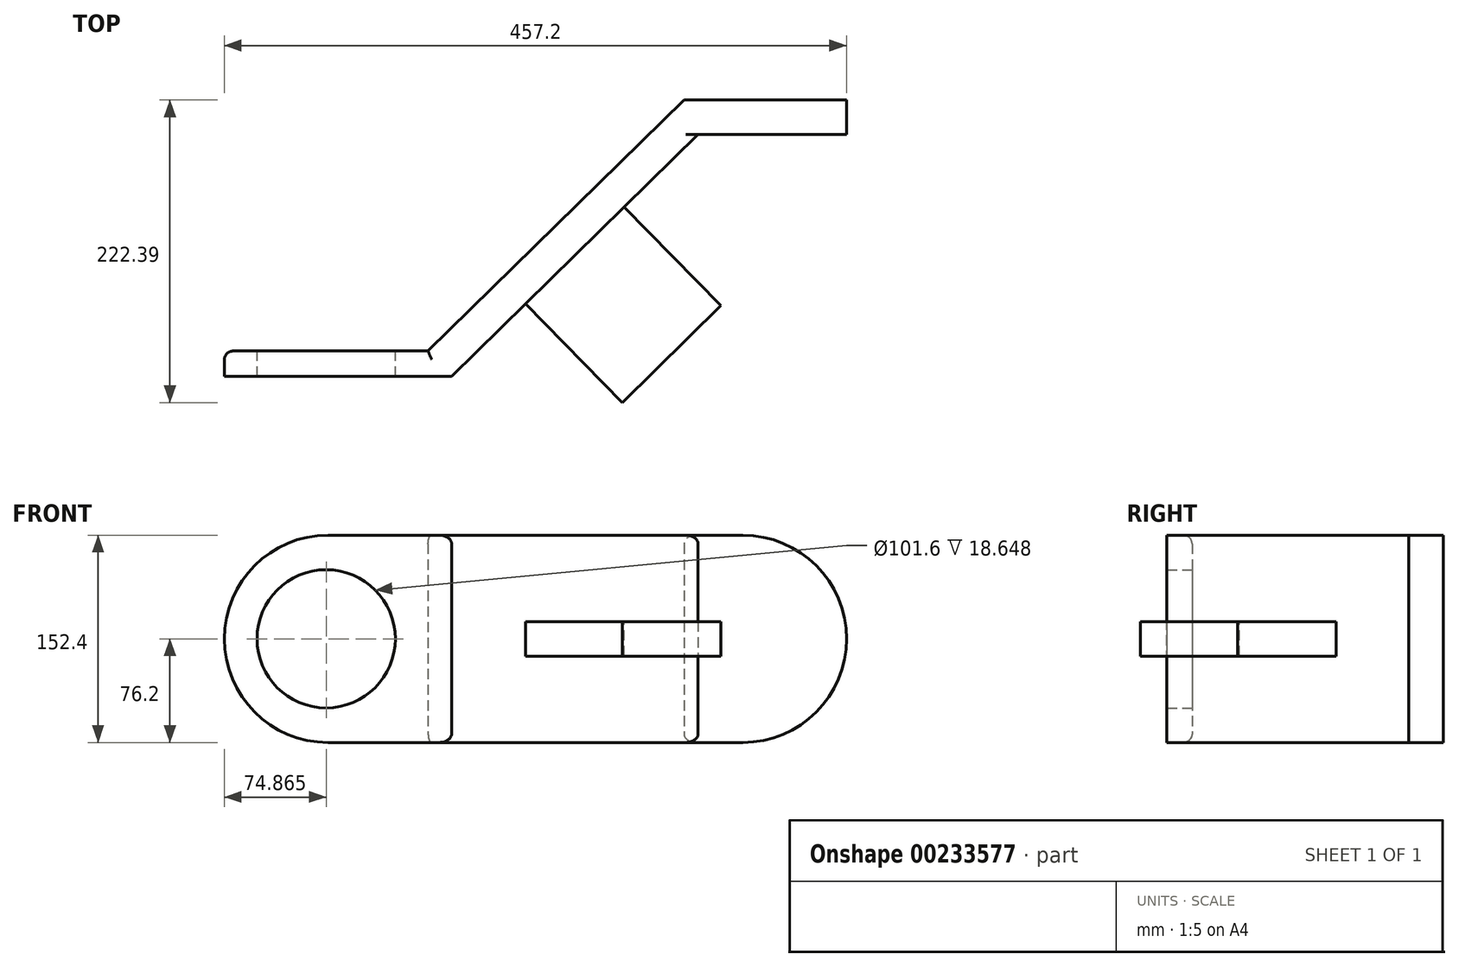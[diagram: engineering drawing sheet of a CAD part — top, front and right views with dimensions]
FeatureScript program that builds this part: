
annotation { "Feature Type Name" : "Feature", "Feature Type Description" : "" }
export const myFeature = defineFeature(function(context is Context, id is Id, definition is map)
    precondition{}
    {
        {
            var Q0;
            Q0=qCreatedBy(makeId("Top.planeOp"),FACE);
            var sketch = newSketch(context, id + "F0", { "sketchPlane" : qUnion([Q0])});
            skLineSegment(sketch, "E0.bottom", {"start": v(228.6, -101.6) * mm, "end": v(-228.6, -101.6) * mm});
            skLineSegment(sketch, "E0.top", {"start": v(228.6, 101.6) * mm, "end": v(-228.6, 101.6) * mm});
            skLineSegment(sketch, "E0.left", {"start": v(228.6, -101.6) * mm, "end": v(228.6, 101.6) * mm});
            skLineSegment(sketch, "E0.right", {"start": v(-228.6, -101.6) * mm, "end": v(-228.6, 101.6) * mm});
            skPoint(sketch, "E0.middle", {"position": v(0, 0) * mm});
            skLineSegment(sketch, "E1", {"start": v(228.6, 101.6) * mm, "end": v(36.67, 101.6) * mm});
            skLineSegment(sketch, "E2", {"start": v(-78.87, -82.95) * mm, "end": v(-228.6, -82.95) * mm});
            skLineSegment(sketch, "E3", {"start": v(-78.87, -82.95) * mm, "end": v(109.12, 101.6) * mm});
            skLineSegment(sketch, "E4.0", {"start": v(228.6, 76.2) * mm, "end": v(119.5, 76.2) * mm});
            skLineSegment(sketch, "E5.0", {"start": v(-61.6, -101.6) * mm, "end": v(121.27, 77.93) * mm});
            skSolve(sketch);
        }
        {
            var Q0;
            {var subQ7=sQuery(id+"F0.wireOp",EDGE,"E2");Q0=makeQuery(id+"F0.imprint","IMPRINT",FACE,{"disambiguationData":[TD([[makeQuery(id+"F0.imprint","IMPRINT",EDGE,{"derivedFrom":subQ7}),1.0]])]});}
            extrude(context, id + "F1", {"entities" : qUnion([Q0]), "depth" : 152.4 * mm});
        }
        {
            var Q0;
            Q0=makeQuery(id+"F1.opExtrude","SWEPT_FACE",FACE,{"disambiguationData":[OSD([sQuery(id+"F0.wireOp",EDGE,"E1")])]});
            var sketch = newSketch(context, id + "F2", { "sketchPlane" : qUnion([Q0])});
            skCircle(sketch, "E6", {"center": v(-168.86, 76.2) * mm, "radius": 38.1 * mm});
            skPoint(sketch, "E6.centerSnap0", {"position": v(-168.86, 0) * mm});
            skPoint(sketch, "E6.centerSnap1", {"position": v(-228.6, 76.2) * mm});
            skSolve(sketch);
        }
        {
            var Q0;
            Q0=makeQuery(id+"F1.opExtrude","SWEPT_FACE",FACE,{"disambiguationData":[OSD([sQuery(id+"F0.wireOp",EDGE,"E2")])]});
            var sketch = newSketch(context, id + "F3", { "sketchPlane" : qUnion([Q0])});
            skCircle(sketch, "E7", {"center": v(153.74, 76.2) * mm, "radius": 50.8 * mm});
            skPoint(sketch, "E7.centerSnap0", {"position": v(228.6, 76.2) * mm});
            skPoint(sketch, "E7.centerSnap1", {"position": v(153.74, 0) * mm});
            skSolve(sketch);
        }
        {
            var Q0;
            Q0=makeQuery(id+"F1.opExtrude","CAP_EDGE",EDGE,{"disambiguationData":[OSD([sQuery(id+"F0.wireOp",EDGE,"E0.left")])],"isStart":true});
            var Q1;
            Q1=makeQuery(id+"F1.opExtrude","CAP_EDGE",EDGE,{"disambiguationData":[OSD([sQuery(id+"F0.wireOp",EDGE,"E0.left")])],"isStart":false});
            fillet(context, id + "F4", {"entities" : qUnion([Q0, Q1]), "radius" : 76.2 * mm, "tangentPropagation" : true, "allowEdgeOverflow" : false});
        }
        {
            var Q0;
            Q0=makeQuery(id+"F1.opExtrude","CAP_EDGE",EDGE,{"disambiguationData":[OSD([sQuery(id+"F0.wireOp",EDGE,"E0.right")])],"isStart":false});
            var Q1;
            Q1=makeQuery(id+"F1.opExtrude","CAP_EDGE",EDGE,{"disambiguationData":[OSD([sQuery(id+"F0.wireOp",EDGE,"E0.right")])],"isStart":true});
            fillet(context, id + "F5", {"entities" : qUnion([Q0, Q1]), "radius" : 76.2 * mm, "tangentPropagation" : true, "allowEdgeOverflow" : false});
        }
        {
            var Q0;
            Q0=makeQuery(id+"F3.imprint","IMPRINT",FACE,{"disambiguationData":[TD([[makeQuery(id+"F3.imprint","IMPRINT",EDGE,{"derivedFrom":sQuery(id+"F3.wireOp",EDGE,"E7")}),1.0]])]});
            var Q1;
            Q1=makeQuery(id+"F2.imprint","IMPRINT",FACE,{"disambiguationData":[TD([[makeQuery(id+"F2.imprint","IMPRINT",EDGE,{"derivedFrom":sQuery(id+"F2.wireOp",EDGE,"E6")}),1.0]])]});
            extrude(context, id + "F6", {"entities" : qUnion([Q0, Q1]), "operationType" : NewBodyOperationType.REMOVE, "endBound" : BoundingType.THROUGH_ALL, "oppositeDirection" : true, "depth" : 25.4 * mm});
        }
        {
            var Q0;
            Q0=makeQuery(id+"F1.opExtrude","CAP_EDGE",EDGE,{"disambiguationData":[OSD([sQuery(id+"F0.wireOp",EDGE,"E3")])],"isStart":true});
            var Q1;
            Q1=makeQuery(id+"F1.opExtrude","CAP_EDGE",EDGE,{"disambiguationData":[OSD([sQuery(id+"F0.wireOp",EDGE,"E1")])],"isStart":true});
            var Q2;
            Q2=makeQuery(id+"F4.opFillet","BLEND_EDGE",EDGE,{"blendedFrom":[makeQuery(id+"F1.opExtrude","CAP_EDGE",EDGE,{"disambiguationData":[OSD([sQuery(id+"F0.wireOp",EDGE,"E0.left")])],"isStart":false}),makeQuery(id+"F1.opExtrude","SWEPT_FACE",FACE,{"disambiguationData":[OSD([sQuery(id+"F0.wireOp",EDGE,"E1")])]})],"blendedInto":[makeQuery(id+"F1.opExtrude","SWEPT_FACE",FACE,{"disambiguationData":[OSD([sQuery(id+"F0.wireOp",EDGE,"E1")])]})]});
            var Q3;
            Q3=makeQuery(id+"F1.opExtrude","CAP_EDGE",EDGE,{"disambiguationData":[OSD([sQuery(id+"F0.wireOp",EDGE,"E1")])],"isStart":false});
            var Q4;
            Q4=makeQuery(id+"F1.opExtrude","CAP_EDGE",EDGE,{"disambiguationData":[OSD([sQuery(id+"F0.wireOp",EDGE,"E3")])],"isStart":false});
            var Q5;
            Q5=makeQuery(id+"F1.opExtrude","CAP_EDGE",EDGE,{"disambiguationData":[OSD([sQuery(id+"F0.wireOp",EDGE,"E2")])],"isStart":false});
            var Q6;
            Q6=makeQuery(id+"F5.opFillet","BLEND_EDGE",EDGE,{"blendedFrom":[makeQuery(id+"F1.opExtrude","CAP_EDGE",EDGE,{"disambiguationData":[OSD([sQuery(id+"F0.wireOp",EDGE,"E0.right")])],"isStart":false}),makeQuery(id+"F1.opExtrude","SWEPT_FACE",FACE,{"disambiguationData":[OSD([sQuery(id+"F0.wireOp",EDGE,"E2")])]})],"blendedInto":[makeQuery(id+"F1.opExtrude","SWEPT_FACE",FACE,{"disambiguationData":[OSD([sQuery(id+"F0.wireOp",EDGE,"E2")])]})]});
            var Q7;
            Q7=makeQuery(id+"F5.opFillet","BLEND_EDGE",EDGE,{"blendedFrom":[makeQuery(id+"F1.opExtrude","CAP_EDGE",EDGE,{"disambiguationData":[OSD([sQuery(id+"F0.wireOp",EDGE,"E0.right")])],"isStart":false}),makeQuery(id+"F1.opExtrude","SWEPT_FACE",FACE,{"disambiguationData":[OSD([sQuery(id+"F0.wireOp",EDGE,"E0.bottom")])]})],"blendedInto":[makeQuery(id+"F1.opExtrude","SWEPT_FACE",FACE,{"disambiguationData":[OSD([sQuery(id+"F0.wireOp",EDGE,"E0.bottom")])]})]});
            var Q8;
            Q8=makeQuery(id+"F1.opExtrude","CAP_EDGE",EDGE,{"disambiguationData":[OSD([sQuery(id+"F0.wireOp",EDGE,"E5.0")])],"isStart":true});
            var Q9;
            Q9=makeQuery(id+"F4.opFillet","BLEND_EDGE",EDGE,{"blendedFrom":[makeQuery(id+"F1.opExtrude","CAP_EDGE",EDGE,{"disambiguationData":[OSD([sQuery(id+"F0.wireOp",EDGE,"E0.left")])],"isStart":false}),makeQuery(id+"F1.opExtrude","SWEPT_FACE",FACE,{"disambiguationData":[OSD([sQuery(id+"F0.wireOp",EDGE,"E4.0")])]})],"blendedInto":[makeQuery(id+"F1.opExtrude","SWEPT_FACE",FACE,{"disambiguationData":[OSD([sQuery(id+"F0.wireOp",EDGE,"E4.0")])]})]});
            var Q10;
            Q10=makeQuery(id+"F1.opExtrude","CAP_EDGE",EDGE,{"disambiguationData":[OSD([sQuery(id+"F0.wireOp",EDGE,"E5.0")])],"isStart":false});
            fillet(context, id + "F7", {"entities" : qUnion([Q0, Q1, Q2, Q3, Q4, Q5, Q6, Q7, Q8, Q9, Q10]), "radius" : 6.35 * mm, "tangentPropagation" : true, "allowEdgeOverflow" : false});
        }
        {
            var Q0;
            Q0=makeQuery(id+"F1.opExtrude","SWEPT_FACE",FACE,{"disambiguationData":[OSD([sQuery(id+"F0.wireOp",EDGE,"E5.0")])]});
            var sketch = newSketch(context, id + "F8", { "sketchPlane" : qUnion([Q0])});
            skLineSegment(sketch, "E8.bottom", {"start": v(62.56, 63.5) * mm, "end": v(-39.04, 63.5) * mm});
            skLineSegment(sketch, "E8.top", {"start": v(62.56, 88.9) * mm, "end": v(-39.04, 88.9) * mm});
            skLineSegment(sketch, "E8.left", {"start": v(62.56, 63.5) * mm, "end": v(62.56, 88.9) * mm});
            skLineSegment(sketch, "E8.right", {"start": v(-39.04, 63.5) * mm, "end": v(-39.04, 88.9) * mm});
            skPoint(sketch, "E8.middle", {"position": v(11.76, 76.2) * mm});
            skPoint(sketch, "E8.middle.positionSnap0", {"position": v(-115.14, 76.2) * mm});
            skPoint(sketch, "E8.middle.positionSnap1", {"position": v(11.76, 6.35) * mm});
            skPoint(sketch, "E8.centerSnap0", {"position": v(-115.14, 76.2) * mm});
            skPoint(sketch, "E8.centerSnap1", {"position": v(11.76, 6.35) * mm});
            skSolve(sketch);
        }
        {
            var Q0;
            Q0=makeQuery(id+"F8.imprint","IMPRINT",FACE,{"disambiguationData":[TD([[makeQuery(id+"F8.imprint","IMPRINT",EDGE,{"derivedFrom":sQuery(id+"F8.wireOp",EDGE,"E8.bottom")}),-1.0]])]});
            extrude(context, id + "F9", {"entities" : qUnion([Q0]), "operationType" : NewBodyOperationType.ADD, "depth" : 101.6 * mm});
        }
    });
